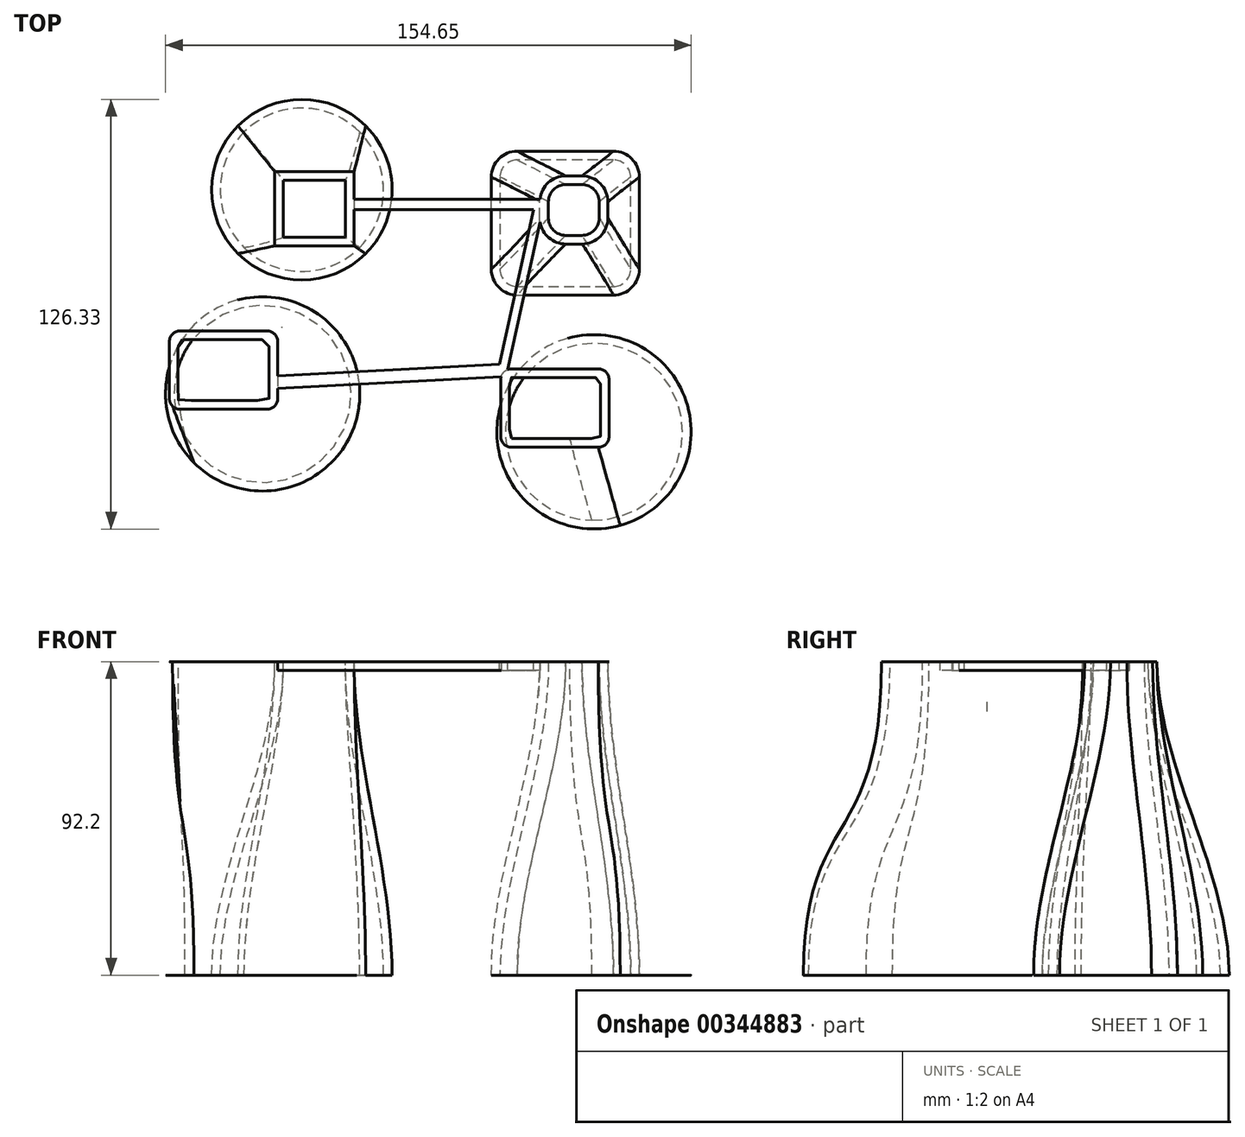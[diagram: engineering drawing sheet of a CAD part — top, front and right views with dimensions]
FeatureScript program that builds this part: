
annotation { "Feature Type Name" : "Feature", "Feature Type Description" : "" }
export const myFeature = defineFeature(function(context is Context, id is Id, definition is map)
    precondition{}
    {
        {
            var Q0;
            Q0=qCreatedBy(makeId("Top.planeOp"),FACE);
            cPlane(context, id + "F0", {"entities" : qUnion([Q0]), "cplaneType" : CPlaneType.OFFSET, "offset" : 92.2 * mm, "width" : 152.4 * mm, "height" : 152.4 * mm});
        }
        {
            var Q0;
            Q0=qCreatedBy(makeId("Top.planeOp"),FACE);
            var sketch = newSketch(context, id + "F1", { "sketchPlane" : qUnion([Q0])});
            skLineSegment(sketch, "E0.bottom", {"start": v(0, 0) * mm, "end": v(43.54, 0) * mm});
            skLineSegment(sketch, "E0.top", {"start": v(0, 42.3) * mm, "end": v(43.54, 42.3) * mm});
            skLineSegment(sketch, "E0.left", {"start": v(0, 0) * mm, "end": v(0, 42.3) * mm});
            skLineSegment(sketch, "E0.right", {"start": v(43.54, 0) * mm, "end": v(43.54, 42.3) * mm});
            skSolve(sketch);
        }
        {
            var Q0;
            Q0=qCreatedBy(id+"F0.planeOp",FACE);
            var sketch = newSketch(context, id + "F2", { "sketchPlane" : qUnion([Q0])});
            skLineSegment(sketch, "E1.bottom", {"start": v(14.26, 15.02) * mm, "end": v(34.28, 15.02) * mm});
            skLineSegment(sketch, "E1.top", {"start": v(14.26, 35.04) * mm, "end": v(34.28, 35.04) * mm});
            skLineSegment(sketch, "E1.left", {"start": v(14.26, 15.02) * mm, "end": v(14.26, 35.04) * mm});
            skLineSegment(sketch, "E1.right", {"start": v(34.28, 15.02) * mm, "end": v(34.28, 35.04) * mm});
            skSolve(sketch);
        }
        {
            var Q0;
            Q0=makeQuery(id+"F1.imprint","IMPRINT",FACE,{"disambiguationData":[TD([[makeQuery(id+"F1.imprint","IMPRINT",EDGE,{"derivedFrom":sQuery(id+"F1.wireOp",EDGE,"E0.bottom")}),1.0]])]});
            var Q1;
            Q1=makeQuery(id+"F2.imprint","IMPRINT",FACE,{"disambiguationData":[TD([[makeQuery(id+"F2.imprint","IMPRINT",EDGE,{"derivedFrom":sQuery(id+"F2.wireOp",EDGE,"E1.bottom")}),1.0]])]});
            loft(context, id + "F3", {"startCondition" : LoftEndDerivativeType.NORMAL_TO_PROFILE, "startMagnitude" : 1, "endCondition" : LoftEndDerivativeType.NORMAL_TO_PROFILE, "endMagnitude" : 1, "sheetProfilesArray" : [{ "sheetProfileEntities" : qUnion([Q0]) }, { "sheetProfileEntities" : qUnion([Q1]) }]});
        }
        {
            var Q0;
            Q0=qCreatedBy(makeId("Top.planeOp"),FACE);
            var sketch = newSketch(context, id + "F4", { "sketchPlane" : qUnion([Q0])});
            skCircle(sketch, "E2", {"center": v(-55.76, 30.98) * mm, "radius": 26.56 * mm});
            skPoint(sketch, "E3", {"position": v(-74.54, 49.76) * mm});
            skPoint(sketch, "E4", {"position": v(-38.5, 51.17) * mm});
            skPoint(sketch, "E5", {"position": v(-77.79, 16.14) * mm});
            skLineSegment(sketch, "E6", {"start": v(-74.54, 49.76) * mm, "end": v(-82.32, 30.98) * mm, "construction": true});
            skLineSegment(sketch, "E7", {"start": v(-74.54, 49.76) * mm, "end": v(-55.76, 57.54) * mm, "construction": true});
            skSolve(sketch);
        }
        {
            var Q0;
            Q0=qCreatedBy(id+"F0.planeOp",FACE);
            var sketch = newSketch(context, id + "F5", { "sketchPlane" : qUnion([Q0])});
            skLineSegment(sketch, "E8.bottom", {"start": v(-63.71, 36.26) * mm, "end": v(-40.39, 36.26) * mm});
            skLineSegment(sketch, "E8.top", {"start": v(-63.71, 14.46) * mm, "end": v(-40.39, 14.46) * mm});
            skLineSegment(sketch, "E8.left", {"start": v(-63.71, 36.26) * mm, "end": v(-63.71, 14.46) * mm});
            skLineSegment(sketch, "E8.right", {"start": v(-40.39, 36.26) * mm, "end": v(-40.39, 14.46) * mm});
            skSolve(sketch);
        }
        {
            var Q0;
            Q0=makeQuery(id+"F4.imprint","IMPRINT",FACE,{"disambiguationData":[TD([[makeQuery(id+"F4.imprint","IMPRINT",EDGE,{"derivedFrom":sQuery(id+"F4.wireOp",EDGE,"E2")}),1.0]])]});
            var Q1;
            Q1=makeQuery(id+"F5.imprint","IMPRINT",FACE,{"disambiguationData":[TD([[makeQuery(id+"F5.imprint","IMPRINT",EDGE,{"derivedFrom":sQuery(id+"F5.wireOp",EDGE,"E8.bottom")}),-1.0]])]});
            var Q2;
            Q2=sQuery(id+"F5.wireOp",VERTEX,"E8.left.start");
            var Q3;
            Q3=sQuery(id+"F4.wireOp",VERTEX,"E3");
            loft(context, id + "F6", {"startCondition" : LoftEndDerivativeType.NORMAL_TO_PROFILE, "startMagnitude" : 1, "endCondition" : LoftEndDerivativeType.NORMAL_TO_PROFILE, "endMagnitude" : 1, "sheetProfilesArray" : [{ "sheetProfileEntities" : qUnion([Q0]) }, { "sheetProfileEntities" : qUnion([Q1]) }], "matchConnections" : true, "connections" : [{ "connectionEntities" : qUnion([Q2, Q3]), "connectionEdgeQueries" : qUnion([]), "connectionEdgeParameters" : [] }]});
        }
        {
            var Q0;
            Q0=makeQuery(id+"F3.opLoft","SWEPT_EDGE",EDGE,{"disambiguationData":[OSD([sQuery(id+"F1.wireOp",EDGE,"E0.bottom"),sQuery(id+"F1.wireOp",EDGE,"E0.right"),sQuery(id+"F2.wireOp",EDGE,"E1.bottom"),sQuery(id+"F2.wireOp",EDGE,"E1.right")])]});
            var Q1;
            Q1=makeQuery(id+"F3.opLoft","SWEPT_EDGE",EDGE,{"disambiguationData":[OSD([sQuery(id+"F1.wireOp",EDGE,"E0.bottom"),sQuery(id+"F1.wireOp",EDGE,"E0.left"),sQuery(id+"F2.wireOp",EDGE,"E1.bottom"),sQuery(id+"F2.wireOp",EDGE,"E1.left")])]});
            var Q2;
            Q2=makeQuery(id+"F3.opLoft","SWEPT_EDGE",EDGE,{"disambiguationData":[OSD([sQuery(id+"F1.wireOp",EDGE,"E0.top"),sQuery(id+"F1.wireOp",EDGE,"E0.left"),sQuery(id+"F2.wireOp",EDGE,"E1.top"),sQuery(id+"F2.wireOp",EDGE,"E1.left")])]});
            var Q3;
            Q3=makeQuery(id+"F3.opLoft","SWEPT_EDGE",EDGE,{"disambiguationData":[OSD([sQuery(id+"F1.wireOp",EDGE,"E0.top"),sQuery(id+"F1.wireOp",EDGE,"E0.right"),sQuery(id+"F2.wireOp",EDGE,"E1.top"),sQuery(id+"F2.wireOp",EDGE,"E1.right")])]});
            fillet(context, id + "F7", {"entities" : qUnion([Q0, Q1, Q2, Q3]), "radius" : 7.62 * mm, "tangentPropagation" : true, "allowEdgeOverflow" : false});
        }
        {
            var Q0;
            Q0=makeQuery(id+"F6.opLoft","CAP_FACE",FACE,{"disambiguationData":[OSD([makeQuery(id+"F4.imprint","IMPRINT",FACE,{"disambiguationData":[TD([[makeQuery(id+"F4.imprint","IMPRINT",EDGE,{"derivedFrom":sQuery(id+"F4.wireOp",EDGE,"E2")}),1.0]])]})])],"isStart":true});
            var Q1;
            Q1=makeQuery(id+"F3.opLoft","CAP_FACE",FACE,{"disambiguationData":[OSD([makeQuery(id+"F1.imprint","IMPRINT",FACE,{"disambiguationData":[TD([[makeQuery(id+"F1.imprint","IMPRINT",EDGE,{"derivedFrom":sQuery(id+"F1.wireOp",EDGE,"E0.bottom")}),1.0]])]})])],"isStart":true});
            var Q2;
            Q2=makeQuery(id+"F6.opLoft","CAP_FACE",FACE,{"disambiguationData":[OSD([makeQuery(id+"F5.imprint","IMPRINT",FACE,{"disambiguationData":[TD([[makeQuery(id+"F5.imprint","IMPRINT",EDGE,{"derivedFrom":sQuery(id+"F5.wireOp",EDGE,"E8.bottom")}),-1.0]])]})])],"isStart":true});
            var Q3;
            Q3=makeQuery(id+"F3.opLoft","CAP_FACE",FACE,{"disambiguationData":[OSD([makeQuery(id+"F2.imprint","IMPRINT",FACE,{"disambiguationData":[TD([[makeQuery(id+"F2.imprint","IMPRINT",EDGE,{"derivedFrom":sQuery(id+"F2.wireOp",EDGE,"E1.bottom")}),1.0]])]})])],"isStart":true});
            shell(context, id + "F8", {"entities" : qUnion([Q0, Q1, Q2, Q3]), "thickness" : 2.54 * mm});
        }
        {
            var Q0;
            Q0=qCreatedBy(makeId("Top.planeOp"),FACE);
            var sketch = newSketch(context, id + "F9", { "sketchPlane" : qUnion([Q0])});
            skCircle(sketch, "E9", {"center": v(-67.3, -29.06) * mm, "radius": 28.58 * mm});
            skLineSegment(sketch, "E10", {"start": v(-87.5, -8.86) * mm, "end": v(-47.1, -49.27) * mm, "construction": true});
            skLineSegment(sketch, "E11", {"start": v(-87.5, -49.27) * mm, "end": v(-47.1, -8.86) * mm, "construction": true});
            skLineSegment(sketch, "E12", {"start": v(-87.5, -8.86) * mm, "end": v(-87.5, -49.27) * mm, "construction": true});
            skLineSegment(sketch, "E13", {"start": v(-47.1, -49.27) * mm, "end": v(-87.5, -49.27) * mm, "construction": true});
            skCircle(sketch, "E14", {"center": v(30.2, -40.21) * mm, "radius": 28.58 * mm});
            skLineSegment(sketch, "E15", {"start": v(-67.3, -29.06) * mm, "end": v(30.2, -40.21) * mm, "construction": true});
            skSolve(sketch);
        }
        {
            var Q0;
            Q0=qCreatedBy(id+"F0.planeOp",FACE);
            var sketch = newSketch(context, id + "F10", { "sketchPlane" : qUnion([Q0])});
            skLineSegment(sketch, "E16.bottom", {"start": v(-66.03, -33.6) * mm, "end": v(-91.58, -33.6) * mm});
            skLineSegment(sketch, "E16.top", {"start": v(-66.03, -10.54) * mm, "end": v(-91.58, -10.54) * mm});
            skLineSegment(sketch, "E16.left", {"start": v(-62.85, -30.42) * mm, "end": v(-62.85, -13.71) * mm});
            skLineSegment(sketch, "E16.right", {"start": v(-94.75, -30.42) * mm, "end": v(-94.75, -13.71) * mm});
            skPoint(sketch, "E16.middle", {"position": v(-78.8, -22.07) * mm});
            skPoint(sketch, "E17.visualSharp", {"position": v(-94.75, -10.54) * mm});
            skArc(sketch, "E17.filletArc", {"start": v(-91.58, -10.54) * mm, "mid": v(-93.82, -11.47) * mm, "end": v(-94.75, -13.71) * mm});
            skPoint(sketch, "E18.visualSharp", {"position": v(-94.75, -33.6) * mm});
            skArc(sketch, "E18.filletArc", {"start": v(-94.75, -30.42) * mm, "mid": v(-93.82, -32.67) * mm, "end": v(-91.58, -33.6) * mm});
            skPoint(sketch, "E19.visualSharp", {"position": v(-62.85, -33.6) * mm});
            skArc(sketch, "E19.filletArc", {"start": v(-66.03, -33.6) * mm, "mid": v(-63.78, -32.67) * mm, "end": v(-62.85, -30.42) * mm});
            skPoint(sketch, "E20.visualSharp", {"position": v(-62.85, -10.54) * mm});
            skArc(sketch, "E20.filletArc", {"start": v(-62.85, -13.71) * mm, "mid": v(-63.78, -11.47) * mm, "end": v(-66.03, -10.54) * mm});
            skLineSegment(sketch, "E21.bottom", {"start": v(31.48, -44.75) * mm, "end": v(5.93, -44.75) * mm});
            skLineSegment(sketch, "E21.top", {"start": v(31.48, -21.7) * mm, "end": v(5.93, -21.7) * mm});
            skLineSegment(sketch, "E21.left", {"start": v(34.65, -41.58) * mm, "end": v(34.65, -24.87) * mm});
            skLineSegment(sketch, "E21.right", {"start": v(2.75, -41.58) * mm, "end": v(2.75, -24.87) * mm});
            skPoint(sketch, "E21.middle", {"position": v(18.7, -33.22) * mm});
            skPoint(sketch, "E22.visualSharp", {"position": v(2.75, -21.7) * mm});
            skArc(sketch, "E22.filletArc", {"start": v(5.93, -21.7) * mm, "mid": v(3.68, -22.62) * mm, "end": v(2.75, -24.87) * mm});
            skPoint(sketch, "E23.visualSharp", {"position": v(2.75, -44.75) * mm});
            skArc(sketch, "E23.filletArc", {"start": v(2.75, -41.58) * mm, "mid": v(3.68, -43.82) * mm, "end": v(5.93, -44.75) * mm});
            skPoint(sketch, "E24.visualSharp", {"position": v(34.65, -44.75) * mm});
            skArc(sketch, "E24.filletArc", {"start": v(31.48, -44.75) * mm, "mid": v(33.72, -43.82) * mm, "end": v(34.65, -41.58) * mm});
            skPoint(sketch, "E25.visualSharp", {"position": v(34.65, -21.7) * mm});
            skArc(sketch, "E25.filletArc", {"start": v(34.65, -24.87) * mm, "mid": v(33.72, -22.62) * mm, "end": v(31.48, -21.7) * mm});
            skLineSegment(sketch, "E26", {"start": v(-78.8, -22.07) * mm, "end": v(18.7, -33.22) * mm, "construction": true});
            skPoint(sketch, "E27", {"position": v(-93.82, -32.67) * mm});
            skSolve(sketch);
        }
        {
            var Q0;
            Q0=makeQuery(id+"F9.imprint","IMPRINT",FACE,{"disambiguationData":[TD([[makeQuery(id+"F9.imprint","IMPRINT",EDGE,{"derivedFrom":sQuery(id+"F9.wireOp",EDGE,"E9")}),1.0]])]});
            var Q1;
            Q1=makeQuery(id+"F10.imprint","IMPRINT",FACE,{"disambiguationData":[TD([[makeQuery(id+"F10.imprint","IMPRINT",EDGE,{"derivedFrom":sQuery(id+"F10.wireOp",EDGE,"E16.bottom")}),-1.0]])]});
            var Q2;
            Q2=sQuery(id+"F10.wireOp",VERTEX,"E27");
            var Q3;
            Q3=sQuery(id+"F9.wireOp",VERTEX,"E13.end");
            loft(context, id + "F11", {"startCondition" : LoftEndDerivativeType.NORMAL_TO_PROFILE, "startMagnitude" : 1.6, "endCondition" : LoftEndDerivativeType.NORMAL_TO_PROFILE, "endMagnitude" : 1.8, "sheetProfilesArray" : [{ "sheetProfileEntities" : qUnion([Q0]) }, { "sheetProfileEntities" : qUnion([Q1]) }], "matchConnections" : true, "connections" : [{ "connectionEntities" : qUnion([Q2, Q3]), "connectionEdgeQueries" : qUnion([]), "connectionEdgeParameters" : [] }]});
        }
        {
            var Q0;
            Q0=makeQuery(id+"F9.imprint","IMPRINT",FACE,{"disambiguationData":[TD([[makeQuery(id+"F9.imprint","IMPRINT",EDGE,{"derivedFrom":sQuery(id+"F9.wireOp",EDGE,"E14")}),1.0]])]});
            var Q1;
            Q1=makeQuery(id+"F10.imprint","IMPRINT",FACE,{"disambiguationData":[TD([[makeQuery(id+"F10.imprint","IMPRINT",EDGE,{"derivedFrom":sQuery(id+"F10.wireOp",EDGE,"E21.bottom")}),-1.0]])]});
            loft(context, id + "F12", {"startCondition" : LoftEndDerivativeType.NORMAL_TO_PROFILE, "startMagnitude" : 1.6, "endCondition" : LoftEndDerivativeType.NORMAL_TO_PROFILE, "endMagnitude" : 1.8, "sheetProfilesArray" : [{ "sheetProfileEntities" : qUnion([Q0]) }, { "sheetProfileEntities" : qUnion([Q1]) }]});
        }
        {
            var Q0;
            Q0=makeQuery(id+"F11.opLoft","CAP_FACE",FACE,{"disambiguationData":[OSD([makeQuery(id+"F10.imprint","IMPRINT",FACE,{"disambiguationData":[TD([[makeQuery(id+"F10.imprint","IMPRINT",EDGE,{"derivedFrom":sQuery(id+"F10.wireOp",EDGE,"E16.bottom")}),-1.0]])]})])],"isStart":true});
            var Q1;
            Q1=makeQuery(id+"F11.opLoft","CAP_FACE",FACE,{"disambiguationData":[OSD([makeQuery(id+"F9.imprint","IMPRINT",FACE,{"disambiguationData":[TD([[makeQuery(id+"F9.imprint","IMPRINT",EDGE,{"derivedFrom":sQuery(id+"F9.wireOp",EDGE,"E9")}),1.0]])]})])],"isStart":true});
            var Q2;
            Q2=makeQuery(id+"F12.opLoft","CAP_FACE",FACE,{"disambiguationData":[OSD([makeQuery(id+"F10.imprint","IMPRINT",FACE,{"disambiguationData":[TD([[makeQuery(id+"F10.imprint","IMPRINT",EDGE,{"derivedFrom":sQuery(id+"F10.wireOp",EDGE,"E21.bottom")}),-1.0]])]})])],"isStart":true});
            var Q3;
            Q3=makeQuery(id+"F12.opLoft","CAP_FACE",FACE,{"disambiguationData":[OSD([makeQuery(id+"F9.imprint","IMPRINT",FACE,{"disambiguationData":[TD([[makeQuery(id+"F9.imprint","IMPRINT",EDGE,{"derivedFrom":sQuery(id+"F9.wireOp",EDGE,"E14")}),1.0]])]})])],"isStart":true});
            shell(context, id + "F13", {"entities" : qUnion([Q0, Q1, Q2, Q3]), "thickness" : 2.54 * mm});
        }
        {
            var Q0;
            Q0=qCreatedBy(id+"F0.planeOp",FACE);
            var sketch = newSketch(context, id + "F14", { "sketchPlane" : qUnion([Q0])});
            skLineSegment(sketch, "E28", {"start": v(-41.78, 28.18) * mm, "end": v(15.84, 28.18) * mm});
            skLineSegment(sketch, "E29", {"start": v(15.84, 28.18) * mm, "end": v(4.35, -23.95) * mm});
            skLineSegment(sketch, "E30", {"start": v(4.35, -23.95) * mm, "end": v(-64.02, -27.53) * mm});
            skLineSegment(sketch, "E31", {"start": v(-64.02, -27.53) * mm, "end": v(-64.02, -23.88) * mm});
            skLineSegment(sketch, "E32", {"start": v(-64.02, -23.88) * mm, "end": v(2.45, -20.4) * mm});
            skLineSegment(sketch, "E33", {"start": v(2.45, -20.4) * mm, "end": v(12.48, 25.14) * mm});
            skLineSegment(sketch, "E34", {"start": v(12.48, 25.14) * mm, "end": v(-41.78, 25.14) * mm});
            skLineSegment(sketch, "E35", {"start": v(-41.78, 25.14) * mm, "end": v(-41.78, 28.18) * mm});
            skSolve(sketch);
        }
        {
            var Q0;
            Q0 = qSketchRegion(id + "F14", true);
            extrude(context, id + "F15", {"entities" : qUnion([Q0]), "operationType" : NewBodyOperationType.ADD, "oppositeDirection" : true, "depth" : 2.54 * mm});
        }
    });
